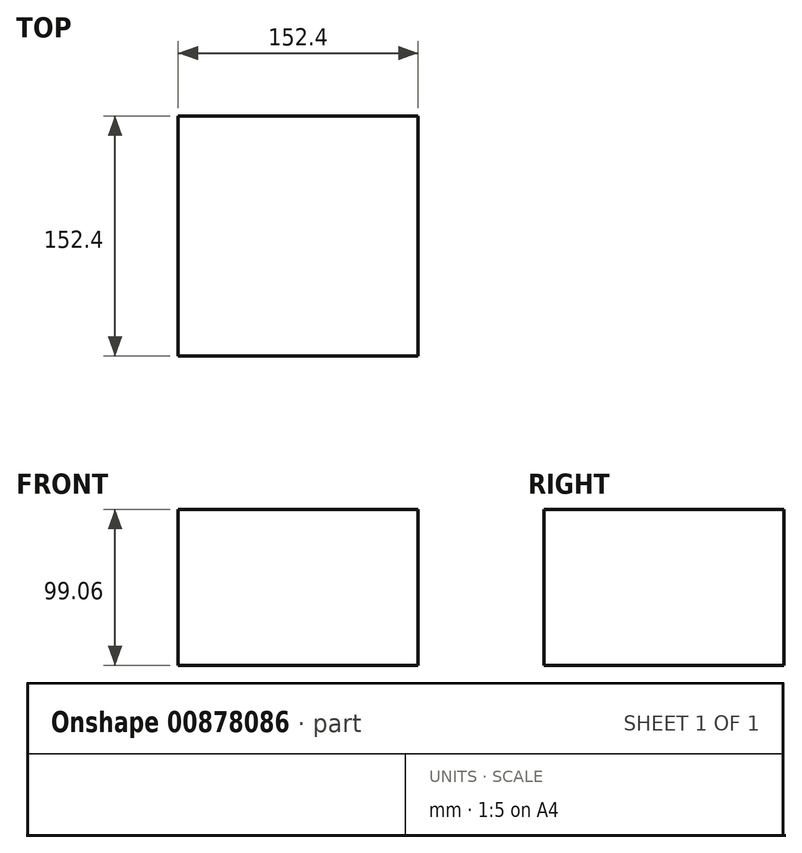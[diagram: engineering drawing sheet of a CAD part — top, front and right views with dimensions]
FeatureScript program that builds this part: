
annotation { "Feature Type Name" : "Feature", "Feature Type Description" : "" }
export const myFeature = defineFeature(function(context is Context, id is Id, definition is map)
    precondition{}
    {
        {
            var Q0;
            Q0=qCreatedBy(makeId("Top.planeOp"),FACE);
            var sketch = newSketch(context, id + "F0", { "sketchPlane" : qUnion([Q0])});
            skLineSegment(sketch, "E0.bottom", {"start": v(0, 0) * mm, "end": v(152.4, 0) * mm});
            skLineSegment(sketch, "E0.top", {"start": v(0, 152.4) * mm, "end": v(152.4, 152.4) * mm});
            skLineSegment(sketch, "E0.left", {"start": v(0, 0) * mm, "end": v(0, 152.4) * mm});
            skLineSegment(sketch, "E0.right", {"start": v(152.4, 0) * mm, "end": v(152.4, 152.4) * mm});
            skSolve(sketch);
        }
        {
            var Q0;
            Q0=makeQuery(id+"F0.imprint","IMPRINT",FACE,{"disambiguationData":[TD([[makeQuery(id+"F0.imprint","IMPRINT",EDGE,{"derivedFrom":sQuery(id+"F0.wireOp",EDGE,"E0.bottom")}),1.0]])]});
            extrude(context, id + "F1", {"entities" : qUnion([Q0]), "depth" : 99.06 * mm, "offsetDistance" : 25.4 * mm});
        }
    });
